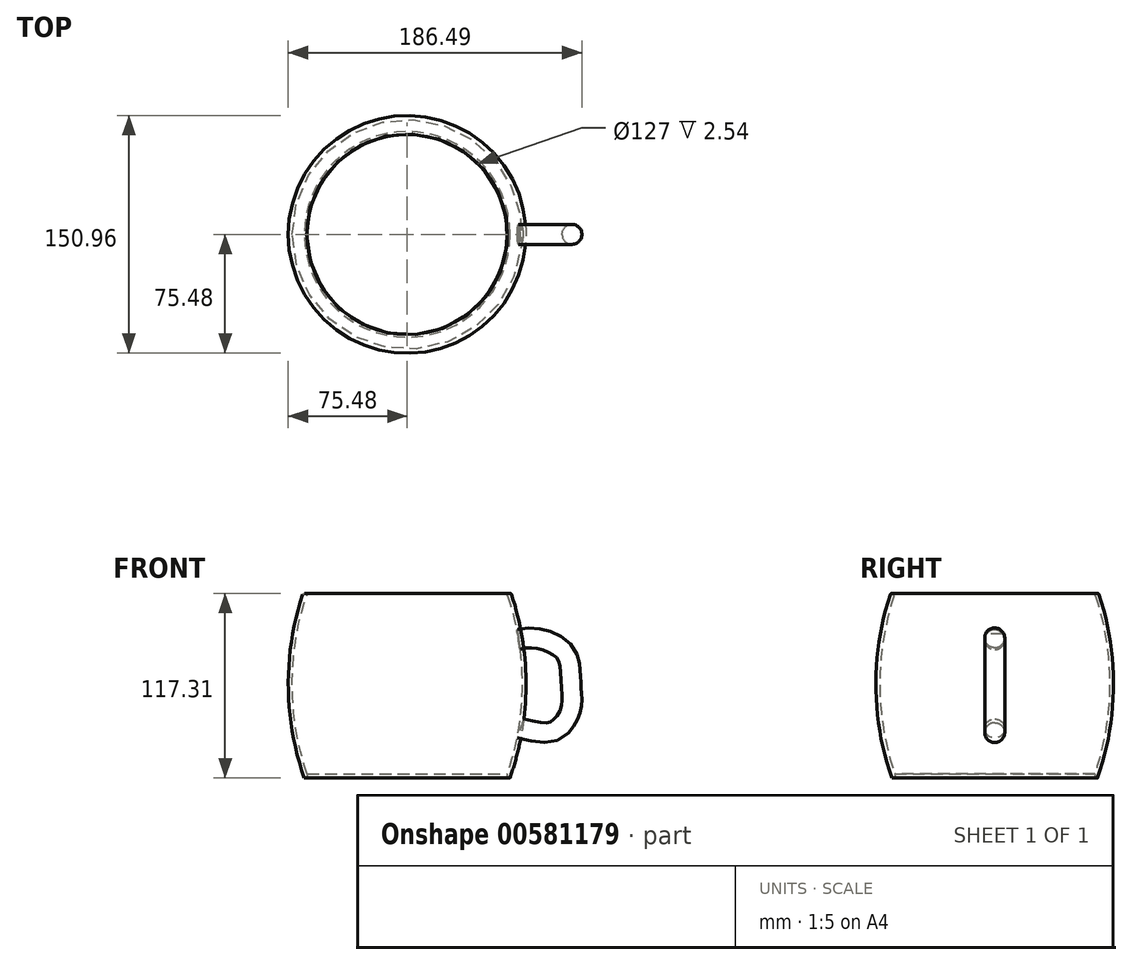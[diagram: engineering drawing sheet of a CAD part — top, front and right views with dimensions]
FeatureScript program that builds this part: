
annotation { "Feature Type Name" : "Feature", "Feature Type Description" : "" }
export const myFeature = defineFeature(function(context is Context, id is Id, definition is map)
    precondition{}
    {
        {
            var Q0;
            Q0=qCreatedBy(makeId("Front.planeOp"),FACE);
            var sketch = newSketch(context, id + "F0", { "sketchPlane" : qUnion([Q0])});
            skLineSegment(sketch, "E0.bottom", {"start": v(0, 0) * mm, "end": v(63.5, 0) * mm});
            skLineSegment(sketch, "E0.top", {"start": v(0, 2.54) * mm, "end": v(63.5, 2.54) * mm});
            skLineSegment(sketch, "E0.left", {"start": v(0, 0) * mm, "end": v(0, 2.54) * mm});
            skLineSegment(sketch, "E0.right", {"start": v(63.5, 0) * mm, "end": v(63.5, 2.54) * mm});
            skSolve(sketch);
        }
        {
            var Q0;
            Q0=qCreatedBy(makeId("Front.planeOp"),FACE);
            var sketch = newSketch(context, id + "F1", { "sketchPlane" : qUnion([Q0])});
            skArc(sketch, "E1", {"start": v(63.5, 2.54) * mm, "mid": v(72.94, 59.7) * mm, "end": v(63.5, 116.84) * mm});
            skArc(sketch, "E2.0", {"start": v(65.31, 0) * mm, "mid": v(75.47, 58.78) * mm, "end": v(65.9, 117.66) * mm});
            skLineSegment(sketch, "E3", {"start": v(63.5, 0) * mm, "end": v(65.31, 0) * mm});
            skLineSegment(sketch, "E4", {"start": v(63.5, 116.84) * mm, "end": v(65.9, 117.66) * mm});
            skLineSegment(sketch, "E5", {"start": v(63.5, 2.54) * mm, "end": v(63.5, 0) * mm});
            skSolve(sketch);
        }
        {
            var Q0;
            Q0=qCreatedBy(makeId("Front.planeOp"),FACE);
            var sketch = newSketch(context, id + "F2", { "sketchPlane" : qUnion([Q0])});
            skLineSegment(sketch, "E6", {"start": v(-104.86, 59.7) * mm, "end": v(149.14, 59.7) * mm, "construction": true});
            skSolve(sketch);
        }
        {
            var Q0;
            Q0=qCreatedBy(makeId("Front.planeOp"),FACE);
            var sketch = newSketch(context, id + "F3", { "sketchPlane" : qUnion([Q0])});
            skLineSegment(sketch, "E7", {"start": v(-104.86, 59.7) * mm, "end": v(70.7, 31.53) * mm, "construction": true});
            skLineSegment(sketch, "E8.MirrorCS", {"start": v(-104.86, 59.69) * mm, "end": v(70.7, 87.85) * mm, "construction": true});
            skSolve(sketch);
        }
        {
            var Q0;
            Q0=qCreatedBy(makeId("Front.planeOp"),FACE);
            var sketch = newSketch(context, id + "F4", { "sketchPlane" : qUnion([Q0])});
            skLineSegment(sketch, "E9", {"start": v(0, 0) * mm, "end": v(0, 108.33) * mm, "construction": true});
            skSolve(sketch);
        }
        {
            var Q0;
            Q0=qCreatedBy(makeId("Front.planeOp"),FACE);
            var sketch = newSketch(context, id + "F5", { "sketchPlane" : qUnion([Q0])});
            skLineSegment(sketch, "E10", {"start": v(70.7, 87.85) * mm, "end": v(68.85, 99.33) * mm});
            skSolve(sketch);
        }
        {
            var Q0;
            Q0=sQuery(id+"F3.wireOp",EDGE,"E8.MirrorCS");
            var Q1;
            Q1=sQuery(id+"F5.wireOp",VERTEX,"E10.start");
            cPlane(context, id + "F6", {"entities" : qUnion([Q0, Q1]), "cplaneType" : CPlaneType.LINE_POINT, "offset" : 25.4 * mm, "width" : 152.4 * mm, "height" : 152.4 * mm});
        }
        {
            var Q0;
            Q0=qCreatedBy(id+"F6.planeOp",FACE);
            var sketch = newSketch(context, id + "F7", { "sketchPlane" : qUnion([Q0])});
            skCircle(sketch, "E11", {"center": v(0, 75.54) * mm, "radius": 6.35 * mm});
            skSolve(sketch);
        }
        {
            var Q0;
            Q0=qCreatedBy(makeId("Front.planeOp"),FACE);
            var sketch = newSketch(context, id + "F8", { "sketchPlane" : qUnion([Q0])});
            skFitSpline(sketch, "E12", {"points": [v(70.75, 87.89) * mm, v(88.81, 87.2) * mm, v(101.5, 77.75) * mm, v(104.14, 59.95) * mm, v(103.98, 43.23) * mm, v(92.84, 29.6) * mm, v(71.93, 31.3) * mm], "startDerivative": vector(110.5, 36.72) * mm, "endDerivative": vector(-133.8, 23.16) * mm});
            skSolve(sketch);
        }
        {
            var Q0;
            Q0=makeQuery(id+"F7.imprint","IMPRINT",FACE,{"disambiguationData":[TD([[makeQuery(id+"F7.imprint","IMPRINT",EDGE,{"derivedFrom":sQuery(id+"F7.wireOp",EDGE,"E11")}),1.0]])]});
            extrude(context, id + "F9", {"entities" : qUnion([Q0]), "depth" : 0.5 * mm, "offsetDistance" : 25.4 * mm});
        }
        {
            var Q0;
            Q0=makeQuery(id+"F9.opExtrude","CAP_FACE",FACE,{"disambiguationData":[OSD([sQuery(id+"F7.wireOp",EDGE,"E11")])],"isStart":false});
            var Q1;
            Q1=sQuery(id+"F8.wireOp",EDGE,"E12");
            sweep(context, id + "F10", {"operationType" : NewBodyOperationType.ADD, "profiles" : qUnion([Q0]), "path" : qUnion([Q1])});
        }
        {
            var Q0;
            Q0=makeQuery(id+"F0.imprint","IMPRINT",FACE,{"disambiguationData":[TD([[makeQuery(id+"F0.imprint","IMPRINT",EDGE,{"derivedFrom":sQuery(id+"F0.wireOp",EDGE,"E0.bottom")}),1.0]])]});
            var Q1;
            Q1=sQuery(id+"F4.wireOp",EDGE,"E9");
            revolve(context, id + "F11", {"entities" : qUnion([Q0]), "axis" : qUnion([Q1]), "revolveType" : RevolveType.FULL});
        }
        {
            var Q0;
            Q0=makeQuery(id+"F1.imprint","IMPRINT",FACE,{"disambiguationData":[TD([[makeQuery(id+"F1.imprint","IMPRINT",EDGE,{"derivedFrom":sQuery(id+"F1.wireOp",EDGE,"E1")}),-1.0]])]});
            var Q1;
            Q1=sQuery(id+"F4.wireOp",EDGE,"E9");
            revolve(context, id + "F12", {"entities" : qUnion([Q0]), "axis" : qUnion([Q1]), "revolveType" : RevolveType.FULL});
        }
        {
            var Q0;
            Q0=makeQuery(id+"F12.opRevolve","SWEPT_EDGE",EDGE,{"disambiguationData":[OSD([sQuery(id+"F1.wireOp",EDGE,"E2.0"),sQuery(id+"F1.wireOp",EDGE,"E4")])]});
            var Q1;
            Q1=makeQuery(id+"F12.opRevolve","SWEPT_EDGE",EDGE,{"disambiguationData":[OSD([sQuery(id+"F1.wireOp",EDGE,"E1"),sQuery(id+"F1.wireOp",EDGE,"E4")])]});
            fillet(context, id + "F13", {"entities" : qUnion([Q0, Q1]), "radius" : 1.27 * mm, "tangentPropagation" : true, "allowEdgeOverflow" : false});
        }
    });
